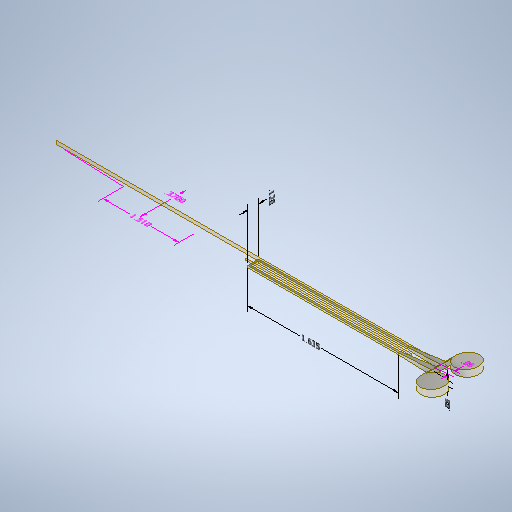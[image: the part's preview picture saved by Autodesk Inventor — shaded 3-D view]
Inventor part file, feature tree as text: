
AUTODESK INVENTOR PART (.ipt)
format: ipt  version: 2025.3 (Build 293356030, 356C)  size: 346,624 bytes
history: native  units: in
note: dims shown in document units (in); Inventor stores cm internally (conversion verified against a paired STEP export)
features: other x8, plane x4, sketch x4, sweep x1, loft x1, mirror x1, extrude x1
ambient origin geometry x8: Origin, YZ Plane, XZ Plane, XY Plane, X Axis, Y Axis, Z Axis, Center Point
bodies: Solid1 (feature_tree)
feature tree (20):
  other  "Annotations"
  sweep  "Sweep1"
  plane  "Work Plane1"
  plane  "Work Plane2"
  plane  "Work Plane4"
  sketch  "Sketch15"  dims[d86=-0.1175in d89=0.1in]
  loft  "Loft3"
  plane  "Work Plane5"
  mirror  "Mirror3"
  extrude  "Extrusion9"  Depth=0.1in
  sketch  "Sketch1"  dims[d6=0.0in d7=0.0in d11=0.375in d19=-0.25in]
  sketch  "Sketch2"  dims[d69=1.625in d70=1.625in]
  other  "Edges4"
  sketch  "Sketch17"  dims[d90=0.0in d91=0.0in d92=0.0in d98=0.02in d99=0.02in d100=0.055in d102=0.055in d104=0.0in d109=0.0in d110=90.0deg d111=0.0in d112=90.0deg d116=-0.06in d127=0.25in d128=0.25in d129=0.375in d132=0.04in d134=0.1875in d135=0.25in d136=0.0in d113=0.0in d114=0.3937in d115=0.12in d120=0.0in d121=0.3937in d122=0.055in d123=0.0in d124=0.3937in d125=0.055in d126=1.635in d42=0.2341in d43=0.169in d44=0.37in d48=0.2141in d49=0.2512in d50=1.51in]
  other  "Linear Dimension 1"
  other  "Linear Dimension 3"
  other  "Linear Dimension 4"
  other  "Linear Dimension 6"
  other  "Linear Dimension 7"
  other  "Linear Dimension 8"
